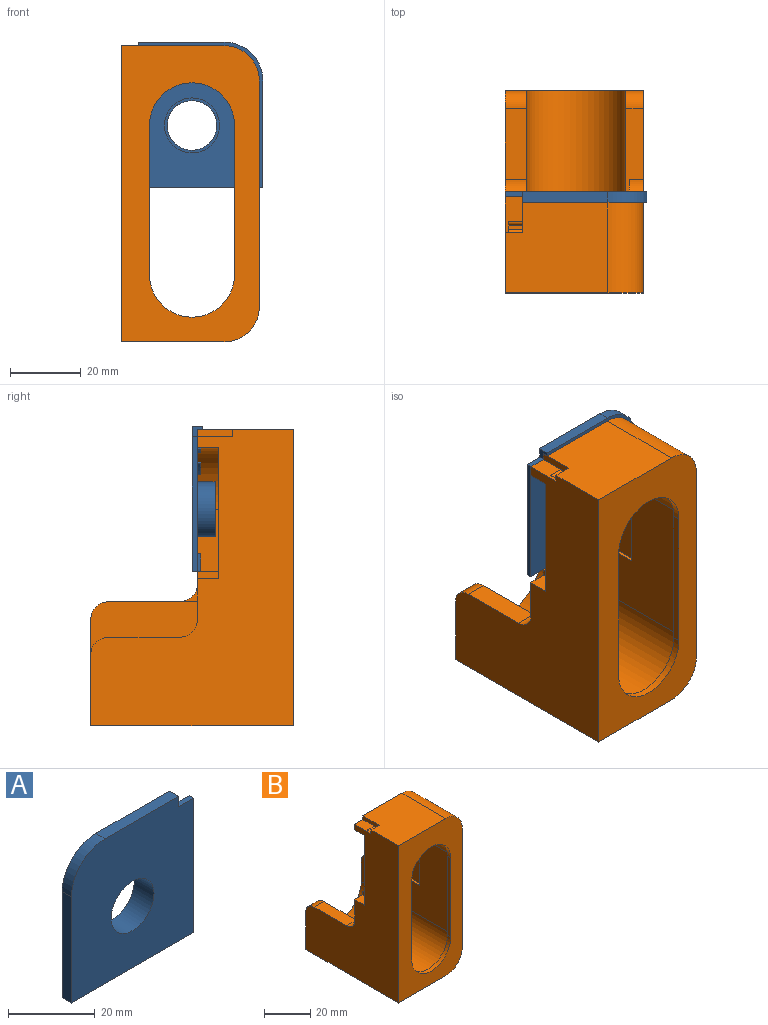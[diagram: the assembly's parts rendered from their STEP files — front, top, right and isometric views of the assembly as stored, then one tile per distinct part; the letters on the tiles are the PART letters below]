
ASSEMBLY  parts=2 mates=1
PART A: 40 faces, bbox 40x6.5x41 mm
  f0: plane 40x39mm, normal (0,1,0), area 1328.1mm2, adj f3,f4,f7,f9,f10,f11,f14,f15
  f1: plane 41x40mm, normal (0,-1,0), area 1445.1mm2, adj f2,f3,f7,f8,f12,f13,f14,f15
  f2: plane 24x3mm, normal (0,0,1), area 72mm2, adj f1,f5,f12,f15
  f3: plane 38x1.5mm, normal (1,0,0), area 57mm2, adj f0,f1,f7,f14
  f4: plane 24x1.5mm, normal (0,0,-1), area 36mm2, adj f0,f5,f11,f15
  f5: plane 41x35mm, normal (0,1,0), area 70.5mm2, adj f2,f4,f7,f10,f11,f12,f13,f15
  f6: plane 15.5x15.5mm, normal (0,1,0), area 34.8mm2, adj f8,f9
  f7: plane 40x3mm, normal (0,0,-1), area 62mm2, adj f0,f1,f3,f5,f10,f13,f21,f23
  f8: cylinder r=7mm len=14mm, axis (0,-1,0), area 285.9mm2, adj f1,f6
  f9: cylinder r=7.75mm len=15.5mm, axis (0,1,0), area 243.5mm2, adj f0,f6
  f10: plane 30x1.5mm, normal (1,0,0), area 45mm2, adj f0,f5,f7,f11
  f11: cylinder r=10mm len=10mm, axis (0,-1,0), area 23.6mm2, adj f0,f4,f5,f10
  f12: cylinder r=11mm len=11mm, axis (0,-1,0), area 51.8mm2, adj f1,f2,f5,f13
  f13: plane 30x3mm, normal (-1,0,0), area 90mm2, adj f1,f5,f7,f12
  f14: plane 5x1.5mm, normal (0,0,1), area 7.5mm2, adj f0,f1,f3,f15
  f15: plane 3x3mm, normal (1,0,0), area 6mm2, adj f0,f1,f2,f4,f5,f14
  f16: plane 1x0.48mm, normal (0.26,0,0.97), area 0.5mm2, adj f0,f17,f19,f20
  f17: cylinder r=17mm len=4.4mm, axis (0,-1,0), area 4.5mm2, adj f0,f16,f18,f20
  f18: plane 1x0.5mm, normal (0,0,-1), area 0.5mm2, adj f0,f17,f19,f20
  f19: cylinder r=17.5mm len=4.53mm, axis (0,-1,0), area 4.6mm2, adj f0,f16,f18,f20
  f20: plane 4.53x1.08mm, normal (0,1,0), area 2.3mm2, adj f16,f17,f18,f19
  f21: plane 5x1mm, normal (-1,0,0), area 5mm2, adj f0,f7,f22,f24
  f22: plane 1x0.5mm, normal (0,0,1), area 0.5mm2, adj f0,f21,f23,f24
  f23: plane 5x1mm, normal (1,0,0), area 5mm2, adj f0,f7,f22,f24
  f24: plane 5x0.5mm, normal (0,1,0), area 2.5mm2, adj f7,f21,f22,f23
  f25: plane 5x1mm, normal (1,0,0), area 5mm2, adj f0,f26,f28,f29
  f26: plane 1x0.5mm, normal (0,0,-1), area 0.5mm2, adj f0,f25,f27,f29
  f27: plane 5x1mm, normal (-1,0,0), area 5mm2, adj f0,f26,f28,f29
  f28: plane 1x0.5mm, normal (0,0,1), area 0.5mm2, adj f0,f25,f27,f29
  f29: plane 5x0.5mm, normal (0,1,0), area 2.5mm2, adj f25,f26,f27,f28
  f30: cylinder r=17mm len=4.33mm, axis (0,-1,0), area 4.5mm2, adj f0,f31,f33,f34
  f31: plane 1x0.47mm, normal (-0.94,0,-0.34), area 0.5mm2, adj f0,f30,f32,f34
  f32: cylinder r=17.5mm len=4.46mm, axis (0,-1,0), area 4.6mm2, adj f0,f31,f33,f34
  f33: plane 1x0.5mm, normal (1,0,0.09), area 0.5mm2, adj f0,f30,f32,f34
  f34: plane 4.5x1.46mm, normal (0,1,0), area 2.3mm2, adj f30,f31,f32,f33
  f35: cylinder r=17mm len=3.27mm, axis (0,-1,0), area 4.5mm2, adj f0,f36,f38,f39
  f36: plane 1x0.41mm, normal (-0.57,0,-0.82), area 0.5mm2, adj f0,f35,f37,f39
  f37: cylinder r=17.5mm len=3.37mm, axis (0,-1,0), area 4.6mm2, adj f0,f36,f38,f39
  f38: plane 1x0.38mm, normal (0.77,0,0.64), area 0.5mm2, adj f0,f35,f37,f39
  f39: plane 3.66x3.41mm, normal (0,1,0), area 2.3mm2, adj f35,f36,f37,f38
PART B: 40 faces, bbox 39x57x83.5 mm
  f0: plane 43.5x39mm, normal (0,1,0), area 383.3mm2, adj f2,f11,f13,f15,f17,f18,f20,f23
  f1: plane 40x4mm, normal (1,0,0), area 84.2mm2, adj f3,f4,f7,f28,f29,f30,f37,f38
  f2: plane 42x10mm, normal (-1,0,0), area 116.2mm2, adj f0,f3,f4,f6,f7,f16,f18,f28
  f3: plane 41x5mm, normal (0,1,0), area 166mm2, adj f1,f2,f13,f18,f30,f38
  f4: plane 4x1mm, normal (0,0,-1), area 4mm2, adj f1,f2,f29,f37
  f5: cylinder r=14mm len=28mm, axis (0,-1,0), area 835.7mm2, adj f10,f14,f32,f37
  f6: plane 13.5x6mm, normal (0,1,0), area 71mm2, adj f2,f7,f13,f14,f16,f24
  f7: plane 9x5mm, normal (0,0,1), area 42mm2, adj f1,f2,f6,f13,f30,f37
  f8: plane 39x30mm, normal (0,1,0), area 472.7mm2, adj f9,f10,f11,f12,f13,f14,f22,f25
  f9: cylinder r=14mm len=55mm, axis (0,-1,0), area 2419mm2, adj f8,f10,f14,f32
  f10: plane 55x42mm, normal (-1,0,0), area 1368.6mm2, adj f5,f8,f9,f21,f26,f32,f37
  f11: plane 63.5x57mm, normal (1,0,0), area 2464.5mm2, adj f0,f8,f21,f22,f23,f26,f27,f31
  f12: plane 57x29mm, normal (0,0,-1), area 1653mm2, adj f8,f13,f22,f31
  f13: plane 83.5x57mm, normal (-1,0,0), area 2762.5mm2, adj f0,f3,f6,f7,f8,f12,f17,f18
  f14: plane 55x42mm, normal (1,0,0), area 1125mm2, adj f5,f6,f8,f9,f16,f19,f24,f25
  f15: cylinder r=17.5mm len=17.5mm, axis (0,-1,0), area 164.9mm2, adj f0,f17,f20,f37
  f16: plane 6x1mm, normal (0,0,1), area 6mm2, adj f2,f6,f14,f37
  f17: plane 17.5x6mm, normal (0,0,-1), area 105mm2, adj f0,f13,f15,f37
  f18: plane 29x27mm, normal (0,0,1), area 733mm2, adj f0,f2,f3,f13,f23,f31
  f19: plane 20x6mm, normal (0,0,1), area 120mm2, adj f13,f14,f24,f25
  f20: plane 26x11mm, normal (-1,0,0), area 161.4mm2, adj f0,f15,f21,f27,f37
  f21: plane 31x5mm, normal (0,0,1), area 111mm2, adj f10,f11,f20,f26,f27,f37
  f22: cylinder r=10mm len=57mm, axis (0,-1,0), area 895.4mm2, adj f8,f11,f12,f31
  f23: cylinder r=10mm len=27mm, axis (0,-1,0), area 424.1mm2, adj f0,f11,f18,f31
  f24: cylinder r=5mm len=6mm, axis (1,0,0), area 47.1mm2, adj f6,f13,f14,f19
  f25: cylinder r=5mm len=6mm, axis (-1,0,0), area 47.1mm2, adj f8,f13,f14,f19
  f26: cylinder r=5mm len=5mm, axis (-1,0,0), area 39.3mm2, adj f8,f10,f11,f21
  f27: cylinder r=5mm len=5mm, axis (-1,0,0), area 31.4mm2, adj f0,f11,f20,f21
  f28: plane 36x4mm, normal (0,-1,0), area 144mm2, adj f1,f2,f29,f39
  f29: cylinder r=1mm len=4mm, axis (-1,0,0), area 6.3mm2, adj f1,f2,f4,f28
  f30: cylinder r=1mm len=4mm, axis (-1,0,0), area 6.3mm2, adj f1,f2,f3,f7
  f31: plane 83.5x39mm, normal (0,-1,0), area 1753.2mm2, adj f11,f12,f13,f18,f22,f23,f33,f34
  f32: plane 70x28mm, normal (0,1,0), area 331.4mm2, adj f5,f9,f10,f14,f33,f34,f35,f36
  f33: cylinder r=12mm len=24mm, axis (0,1,0), area 75.4mm2, adj f31,f32,f34,f36
  f34: plane 42x2mm, normal (-1,0,0), area 84mm2, adj f31,f32,f33,f35
  f35: cylinder r=12mm len=24mm, axis (0,1,0), area 75.4mm2, adj f31,f32,f34,f36
  f36: plane 42x2mm, normal (1,0,0), area 84mm2, adj f31,f32,f33,f35
  f37: plane 43.5x35mm, normal (0,1,0), area 371.9mm2, adj f1,f4,f5,f7,f10,f13,f14,f15
  f38: plane 10x5mm, normal (0,0,1), area 38mm2, adj f0,f1,f2,f3,f13,f39
  f39: cylinder r=1mm len=4mm, axis (1,0,0), area 6.3mm2, adj f1,f2,f28,f38
PLACE A rot(axis=(0,0,1),180deg) t=(-25,25,42)mm
PLACE B at identity fixed
MATE planar B.f0 <-> A.f0  axis (0,1,0) through (-15,25,62.5)mm
